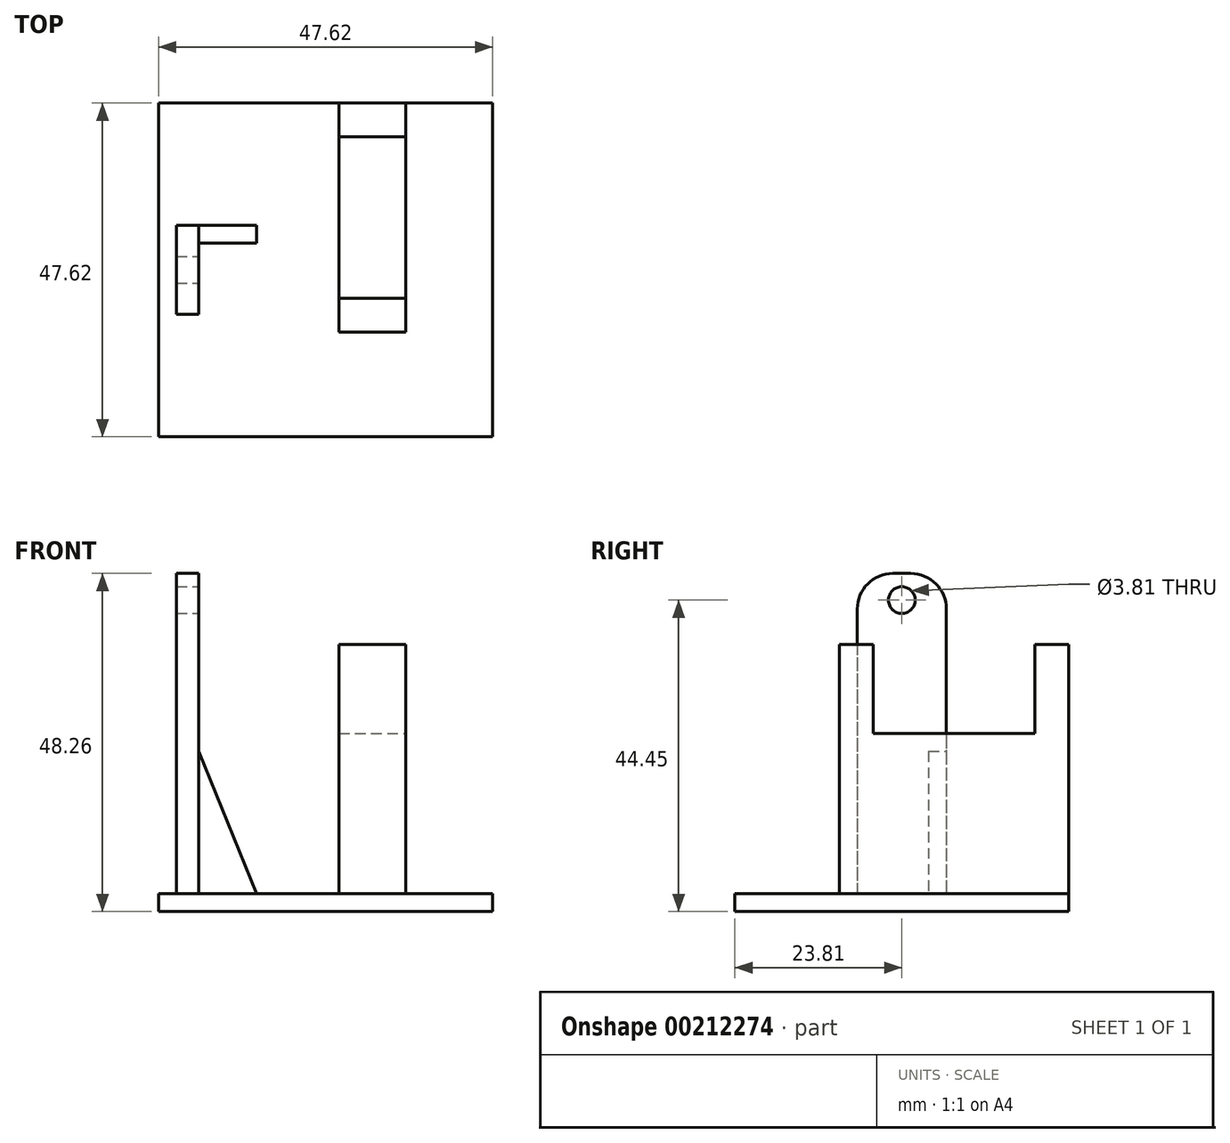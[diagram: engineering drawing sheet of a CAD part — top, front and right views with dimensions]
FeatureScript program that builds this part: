
annotation { "Feature Type Name" : "Feature", "Feature Type Description" : "" }
export const myFeature = defineFeature(function(context is Context, id is Id, definition is map)
    precondition{}
    {
        {
            var Q0;
            Q0=qCreatedBy(makeId("Top.planeOp"),FACE);
            var sketch = newSketch(context, id + "F0", { "sketchPlane" : qUnion([Q0])});
            skLineSegment(sketch, "E0.bottom", {"start": v(23.81, -23.81) * mm, "end": v(-23.81, -23.81) * mm});
            skLineSegment(sketch, "E0.top", {"start": v(23.81, 23.81) * mm, "end": v(-23.81, 23.81) * mm});
            skLineSegment(sketch, "E0.left", {"start": v(23.81, -23.81) * mm, "end": v(23.81, 23.81) * mm});
            skLineSegment(sketch, "E0.right", {"start": v(-23.81, -23.81) * mm, "end": v(-23.81, 23.81) * mm});
            skPoint(sketch, "E0.middle", {"position": v(0, 0) * mm});
            skSolve(sketch);
        }
        {
            var Q0;
            Q0 = qSketchRegion(id + "F0", true);
            extrude(context, id + "F1", {"entities" : qUnion([Q0]), "depth" : 2.54 * mm});
        }
        {
            var Q0;
            Q0=makeQuery(id+"F1.opExtrude","CAP_FACE",FACE,{"disambiguationData":[OSD([sQuery(id+"F0.wireOp",EDGE,"E0.bottom"),sQuery(id+"F0.wireOp",EDGE,"E0.top"),sQuery(id+"F0.wireOp",EDGE,"E0.left"),sQuery(id+"F0.wireOp",EDGE,"E0.right")])],"isStart":false});
            var sketch = newSketch(context, id + "F2", { "sketchPlane" : qUnion([Q0])});
            skLineSegment(sketch, "E1.bottom", {"start": v(11.43, -8.89) * mm, "end": v(1.9, -8.89) * mm});
            skLineSegment(sketch, "E1.top", {"start": v(11.43, 24.13) * mm, "end": v(1.9, 24.13) * mm});
            skLineSegment(sketch, "E1.left", {"start": v(11.43, -8.89) * mm, "end": v(11.43, 24.13) * mm});
            skLineSegment(sketch, "E1.right", {"start": v(1.9, -8.89) * mm, "end": v(1.9, 24.13) * mm});
            skSolve(sketch);
        }
        {
            var Q0;
            Q0=makeQuery(id+"F2.imprint","IMPRINT",FACE,{"disambiguationData":[TD([[makeQuery(id+"F2.imprint","IMPRINT",EDGE,{"derivedFrom":sQuery(id+"F2.wireOp",EDGE,"E1.bottom")}),-1.0]])]});
            var sketch = newSketch(context, id + "F3", { "sketchPlane" : qUnion([Q0])});
            skSolve(sketch);
        }
        {
            var Q0;
            Q0=makeQuery(id+"F3.imprint","IMPRINT",FACE,{"disambiguationData":[TD([[makeQuery(id+"F3.imprint","IMPRINT",EDGE,{"derivedFrom":makeQuery(id+"F2.imprint","IMPRINT",EDGE,{"derivedFrom":sQuery(id+"F2.wireOp",EDGE,"E1.bottom")})}),-1.0]])]});
            extrude(context, id + "F4", {"entities" : qUnion([Q0]), "operationType" : NewBodyOperationType.ADD, "depth" : 22.86 * mm});
        }
        {
            var Q0;
            Q0=makeQuery(id+"F4.opExtrude","CAP_FACE",FACE,{"disambiguationData":[OSD([sQuery(id+"F2.wireOp",EDGE,"E1.bottom"),sQuery(id+"F2.wireOp",EDGE,"E1.top"),sQuery(id+"F2.wireOp",EDGE,"E1.left"),sQuery(id+"F2.wireOp",EDGE,"E1.right")])],"isStart":false});
            var sketch = newSketch(context, id + "F5", { "sketchPlane" : qUnion([Q0])});
            skLineSegment(sketch, "E2.bottom", {"start": v(1.9, -8.89) * mm, "end": v(11.43, -8.89) * mm});
            skLineSegment(sketch, "E2.top", {"start": v(1.9, -4.06) * mm, "end": v(11.43, -4.06) * mm});
            skLineSegment(sketch, "E2.left", {"start": v(1.9, -4.06) * mm, "end": v(1.9, -8.89) * mm});
            skLineSegment(sketch, "E2.right", {"start": v(11.43, -4.06) * mm, "end": v(11.43, -8.89) * mm});
            skLineSegment(sketch, "E3.left", {"start": v(1.9, -8.89) * mm, "end": v(1.9, -4.06) * mm});
            skLineSegment(sketch, "E3.right", {"start": v(11.43, -8.89) * mm, "end": v(11.43, -4.06) * mm});
            skLineSegment(sketch, "E4.bottom", {"start": v(1.9, 23.81) * mm, "end": v(11.43, 23.81) * mm});
            skLineSegment(sketch, "E4.top", {"start": v(1.9, 18.99) * mm, "end": v(11.43, 18.99) * mm});
            skLineSegment(sketch, "E4.left", {"start": v(1.9, 23.81) * mm, "end": v(1.9, 18.99) * mm});
            skLineSegment(sketch, "E4.right", {"start": v(11.43, 23.81) * mm, "end": v(11.43, 18.99) * mm});
            skSolve(sketch);
        }
        {
            var Q0;
            Q0 = qSketchRegion(id + "F5", true);
            extrude(context, id + "F6", {"entities" : qUnion([Q0]), "operationType" : NewBodyOperationType.ADD, "depth" : 12.7 * mm});
        }
        {
            var Q0;
            {var subQ1=sQuery(id+"F2.wireOp",EDGE,"E1.bottom");Q0=makeQuery(id+"F2.imprint","IMPRINT",FACE,{"disambiguationData":[TD([[makeQuery(id+"F2.imprint","IMPRINT",EDGE,{"derivedFrom":subQ1}),1.0]])]});}
            var sketch = newSketch(context, id + "F7", { "sketchPlane" : qUnion([Q0])});
            skLineSegment(sketch, "E5.bottom", {"start": v(-18.1, 6.35) * mm, "end": v(-21.27, 6.35) * mm});
            skLineSegment(sketch, "E5.top", {"start": v(-18.1, -6.35) * mm, "end": v(-21.27, -6.35) * mm});
            skLineSegment(sketch, "E5.left", {"start": v(-18.1, 6.35) * mm, "end": v(-18.1, -6.35) * mm});
            skLineSegment(sketch, "E5.right", {"start": v(-21.27, 6.35) * mm, "end": v(-21.27, -6.35) * mm});
            skPoint(sketch, "E5.middle", {"position": v(-19.69, 0) * mm});
            skSolve(sketch);
        }
        {
            var Q0;
            Q0=makeQuery(id+"F7.imprint","IMPRINT",FACE,{"disambiguationData":[TD([[makeQuery(id+"F7.imprint","IMPRINT",EDGE,{"derivedFrom":sQuery(id+"F7.wireOp",EDGE,"E5.bottom")}),1.0]])]});
            extrude(context, id + "F8", {"entities" : qUnion([Q0]), "operationType" : NewBodyOperationType.ADD, "depth" : 45.72 * mm});
        }
        {
            var Q0;
            Q0=makeQuery(id+"F8.opExtrude","SWEPT_FACE",FACE,{"disambiguationData":[OSD([sQuery(id+"F7.wireOp",EDGE,"E5.left")])]});
            var sketch = newSketch(context, id + "F9", { "sketchPlane" : qUnion([Q0])});
            skCircle(sketch, "E6", {"center": v(0, 44.45) * mm, "radius": 1.9 * mm});
            skSolve(sketch);
        }
        {
            var Q0;
            Q0 = qSketchRegion(id + "F9", true);
            extrude(context, id + "F10", {"entities" : qUnion([Q0]), "operationType" : NewBodyOperationType.REMOVE, "oppositeDirection" : true, "depth" : 25.4 * mm});
        }
        {
            var Q0;
            Q0=makeQuery(id+"F8.opExtrude","CAP_EDGE",EDGE,{"disambiguationData":[OSD([sQuery(id+"F7.wireOp",EDGE,"E5.bottom")])],"isStart":false});
            var Q1;
            Q1=makeQuery(id+"F8.opExtrude","CAP_EDGE",EDGE,{"disambiguationData":[OSD([sQuery(id+"F7.wireOp",EDGE,"E5.top")])],"isStart":false});
            fillet(context, id + "F11", {"entities" : qUnion([Q0, Q1]), "radius" : 5.08 * mm, "tangentPropagation" : true, "allowEdgeOverflow" : false});
        }
        {
            var Q0;
            Q0=makeQuery(id+"F8.opExtrude","SWEPT_FACE",FACE,{"disambiguationData":[OSD([sQuery(id+"F7.wireOp",EDGE,"E5.bottom")])]});
            var sketch = newSketch(context, id + "F12", { "sketchPlane" : qUnion([Q0])});
            skLineSegment(sketch, "E7", {"start": v(18.1, 22.86) * mm, "end": v(9.86, 2.54) * mm});
            skLineSegment(sketch, "E8", {"start": v(9.86, 2.54) * mm, "end": v(18.1, 2.54) * mm});
            skLineSegment(sketch, "E9", {"start": v(18.1, 22.86) * mm, "end": v(18.1, 2.54) * mm});
            skSolve(sketch);
        }
        {
            var Q0;
            Q0=makeQuery(id+"F12.imprint","IMPRINT",FACE,{"disambiguationData":[TD([[makeQuery(id+"F12.imprint","IMPRINT",EDGE,{"derivedFrom":sQuery(id+"F12.wireOp",EDGE,"E7")}),1.0]])]});
            extrude(context, id + "F13", {"entities" : qUnion([Q0]), "operationType" : NewBodyOperationType.ADD, "oppositeDirection" : true, "depth" : 2.54 * mm});
        }
    });
